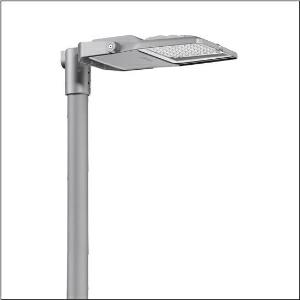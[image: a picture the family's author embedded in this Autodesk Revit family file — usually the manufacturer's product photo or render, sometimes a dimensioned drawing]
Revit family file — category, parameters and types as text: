
# Revit family: floodlight_fl_21_iq_mini___pl61_5xa7771b4c3a_e6c4
name_source: partatom
category: Lighting Fixtures
units: mm (PartAtom-declared; Revit-internal decimal feet)

## family parameters
Cut with Voids When Loaded = No
Host = Face
Light Source = No
Part Type = Normal
Room Calculation Point = No
Round Connector Dimension = Use Diameter
Shared = No

## types (1)
- --- (1 x LED, 6370 lm, 45.5 W, 4000K)
    Apparent Load = 46 VA
    CIE Flux Codes = 33 65 98 100 100
    Color Rendering = 70
    Color Temperature = 4000K
    Default Elevation = 1800 mm
    Description = Floodlight FL 21 iQ mini, floodlight, primary light control with lens, of PMMA, primary optical cover: protective disc, of toughened safety glass, transparent, light distribution: PL61, light emission: direct distribution, installation type: surface-mounted, LED, High Power LED, rated luminous flux: 6.370lm, luminous efficacy: 140lm/W, light colour: 740, colour temperature: 4000K, control: Auto-Match, Temp-Guard, Lumen-Switch, Night-Set, Smart-Wire, Light-Fading, Desk-Remote (wireless, voltage-free reading and setting of iQ features in the workshop via application-optimized NFC function/RFID function), optimised constant luminous flux control (CLO 2.0), with terminal, 6-pole, mains connection: 220..240V, AC, 50/60Hz, start of lifetime: 46W, end of service life: 48W, reduction: 22W, luminaire housing, of diecast aluminium, powder-coated, Siteco® metallic grey (DB 702S), corrosivity category C5 mid according to DIN EN ISO 12944, sealing non-destructively replaceable, please order mast flange separately, mast bracket, of steel, galvanised, powder-coated, Siteco® metallic grey (DB 702S), protection rating (complete): IP66, insulation class (complete): insulation class II (safety insulation), certification: CE, ENEC, VDE, protection symbol: D, impact resistance: IK08, permissible operating ambient temperature: -40..+40°C, permissible operating ambient temperature for outdoor applications: -40..+50°C, standard: DIN EN 12944, LABS conformity tested according to VDMA 24364:2018-05, packaging unit: 1 piece

Light Distribution: PL61
    Height = 70 mm
    Lamp = 1 x LED
    Lamp Light Flux = 6370 lm
    Lamp Power = 45.5 W
    Lamp count = 1
    Length = 485 mm
    Luminous efficacy = 140 lm/W
    Manufacturer = Siteco
    ModVariant = No
    Model = 5XA7771B4C3A
    Number of Poles = 1
    OnlyDefault = Yes
    Power Factor = 1
    Product Name = Floodlight FL 21 iQ mini | PL61
    Product group = floodlight | pylon annexe
    ProductGroupID = 6200
    Protection Class = Protection class II
    Protection Degree = IP 66
    RLX_Detail_Level = 1
    RLX_Emergency_Light_Flux = 0 lm
    RLX_Emergency_Type = 0
    RLX_Emergency_Type_DB = No
    RlxData = <blob elided: 101341 chars, md5=4e391433>
    Socket = socket
    Standby Power = 0 W
    System Light Flux = 6370 lm
    System Power = 46 W
    Type Comments = factory setting: luminous flux: 100 % | dim-lin: 254 | 463 mA
    Type Image = l_1007125.jpg
    URL = http://relux.com
    VarID = @adj_106803
    Voltage = 0 V
    Weight = 0.00 kg
    Width = 337 mm

## geometry (parser evidence)
native form markers: Blend x4, Sweep x11
no freeform markers — native parametric forms only
